# Revit family: Table-Teknion-MXTOT-Oblong_Base-Racetrack-Expansion_Meeting-R2023
name_source: partatom
category: Furniture
units: mm (PartAtom-declared; Revit-internal decimal feet)

## family parameters
Always vertical = Yes
Cut with Voids When Loaded = No
Enable Cutting in Views = No
OmniClass Number = 23.40.20.00
OmniClass Title = General Furniture and Specialties
Render Appearance Source = Family Geometry
Room Calculation Point = No
Shared = Yes
Work Plane-Based = No

## types (3) — shared parameters
(W) Deep Knife Edge (1-3/16") = Yes
Assembly Code = E2020200
Height = 29 "
Manufacturer = Teknion
Manufacturer Fax = 416.661.4586
Product Documentation Link = http://www.teknion.com
Product Line = Expansion Meeting
Product Page URL = https://www.teknion.com
Series = Meeting Tables
Sustainability Data = https://www.teknion.com
URL = www.teknion.com
Unit Weight URL = http://www.teknion.com
Warranty = http://www.teknion.com
zero-valued in all types: Default Elevation

## per-type parameters (varying)
| type | Description | FT | Model | RS |
| (FT) Flush Module - Triple | Oblong Base - Racetrack - Flush Module, Triple | Yes | MXTOT_____FT | No |
| (RS) Recessed Module - Standard | Oblong Base - Racetrack - Recessed Module, Standard | No | MXTOT_____RS | Yes |
| (NN) No Cutout | Oblong Base - Racetrack - No Cutout | No | MXTOT_____NN | No |

## geometry (parser evidence)
native form markers: Sweep x5
no freeform markers — native parametric forms only
